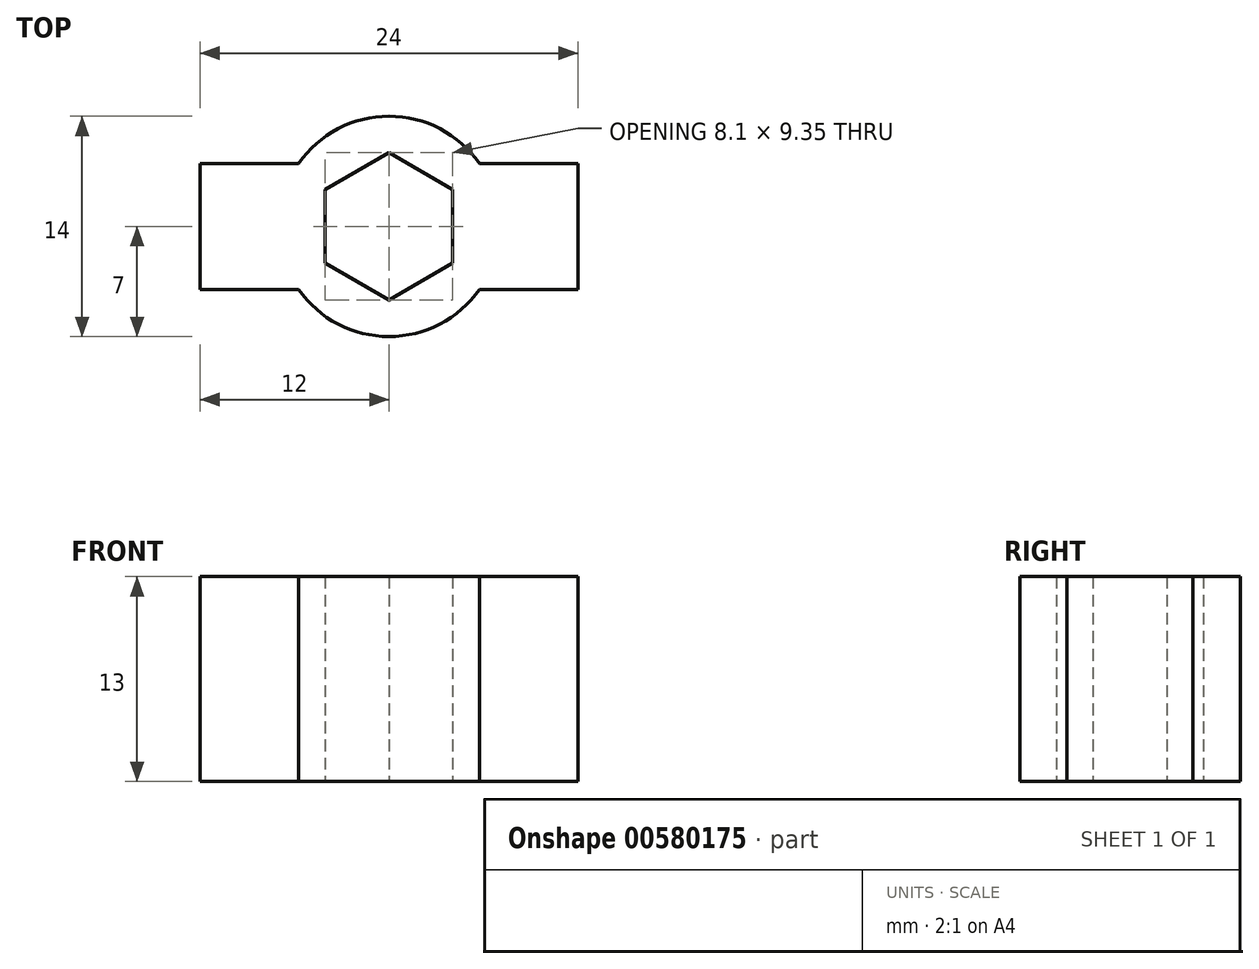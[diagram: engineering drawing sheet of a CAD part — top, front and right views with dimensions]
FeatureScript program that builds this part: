
annotation { "Feature Type Name" : "Feature", "Feature Type Description" : "" }
export const myFeature = defineFeature(function(context is Context, id is Id, definition is map)
    precondition{}
    {
        {
            var Q0;
            Q0=qCreatedBy(makeId("Top.planeOp"),FACE);
            var sketch = newSketch(context, id + "F0", { "sketchPlane" : qUnion([Q0])});
            skCircle(sketch, "E0.cCircle", {"center": v(0, 0) * mm, "radius": 4.05 * mm, "construction": true});
            skLineSegment(sketch, "E0.0", {"start": v(4.05, 2.34) * mm, "end": v(4.05, -2.34) * mm});
            skLineSegment(sketch, "E0.1", {"start": v(4.05, -2.34) * mm, "end": v(0, -4.68) * mm});
            skLineSegment(sketch, "E0.2", {"start": v(0, -4.68) * mm, "end": v(-4.05, -2.34) * mm});
            skLineSegment(sketch, "E0.3", {"start": v(-4.05, -2.34) * mm, "end": v(-4.05, 2.34) * mm});
            skLineSegment(sketch, "E0.4", {"start": v(-4.05, 2.34) * mm, "end": v(0, 4.68) * mm});
            skLineSegment(sketch, "E0.5", {"start": v(0, 4.68) * mm, "end": v(4.05, 2.34) * mm});
            skPoint(sketch, "E0.0.midPoint", {"position": v(4.05, 0) * mm});
            skCircle(sketch, "E1", {"center": v(0, 0) * mm, "radius": 7 * mm});
            skSolve(sketch);
        }
        {
            var Q0;
            Q0=makeQuery(id+"F0.imprint","IMPRINT",FACE,{"disambiguationData":[TD([[makeQuery(id+"F0.imprint","IMPRINT",EDGE,{"derivedFrom":sQuery(id+"F0.wireOp",EDGE,"E0.0")}),1.0]])]});
            extrude(context, id + "F1", {"entities" : qUnion([Q0]), "depth" : 13 * mm, "offsetDistance" : 25 * mm});
        }
        {
            var Q0;
            Q0=makeQuery(id+"F1.opExtrude","CAP_FACE",FACE,{"disambiguationData":[OSD([sQuery(id+"F0.wireOp",EDGE,"E0.0"),sQuery(id+"F0.wireOp",EDGE,"E0.1"),sQuery(id+"F0.wireOp",EDGE,"E0.2"),sQuery(id+"F0.wireOp",EDGE,"E0.3"),sQuery(id+"F0.wireOp",EDGE,"E0.4"),sQuery(id+"F0.wireOp",EDGE,"E0.5"),sQuery(id+"F0.wireOp",EDGE,"E1")])],"isStart":true});
            var sketch = newSketch(context, id + "F2", { "sketchPlane" : qUnion([Q0])});
            skLineSegment(sketch, "E2.bottom", {"start": v(4, -4) * mm, "end": v(12, -4) * mm});
            skLineSegment(sketch, "E2.top", {"start": v(4, 4) * mm, "end": v(12, 4) * mm});
            skLineSegment(sketch, "E2.left", {"start": v(4, -4) * mm, "end": v(4, 4) * mm});
            skLineSegment(sketch, "E2.right", {"start": v(12, -4) * mm, "end": v(12, 4) * mm});
            skLineSegment(sketch, "E3.MirrorCS", {"start": v(-4, 4) * mm, "end": v(-12, 4) * mm});
            skLineSegment(sketch, "E4.MirrorCS", {"start": v(-12, -4) * mm, "end": v(-12, 4) * mm});
            skLineSegment(sketch, "E5.MirrorCS", {"start": v(-4, -4) * mm, "end": v(-4, 4) * mm});
            skLineSegment(sketch, "E6.MirrorCS", {"start": v(-4, -4) * mm, "end": v(-12, -4) * mm});
            skSolve(sketch);
        }
        {
            var Q0;
            {var subQ0=sQuery(id+"F2.wireOp",EDGE,"E2.right");Q0=makeQuery(id+"F2.imprint","IMPRINT",FACE,{"disambiguationData":[TD([[makeQuery(id+"F2.imprint","IMPRINT",EDGE,{"derivedFrom":subQ0}),1.0]])]});}
            var Q1;
            {var subQ0=sQuery(id+"F2.wireOp",EDGE,"E4.MirrorCS");Q1=makeQuery(id+"F2.imprint","IMPRINT",FACE,{"disambiguationData":[TD([[makeQuery(id+"F2.imprint","IMPRINT",EDGE,{"derivedFrom":subQ0}),-1.0]])]});}
            extrude(context, id + "F3", {"entities" : qUnion([Q0, Q1]), "operationType" : NewBodyOperationType.ADD, "oppositeDirection" : true, "depth" : 13 * mm, "offsetDistance" : 25 * mm});
        }
    });
